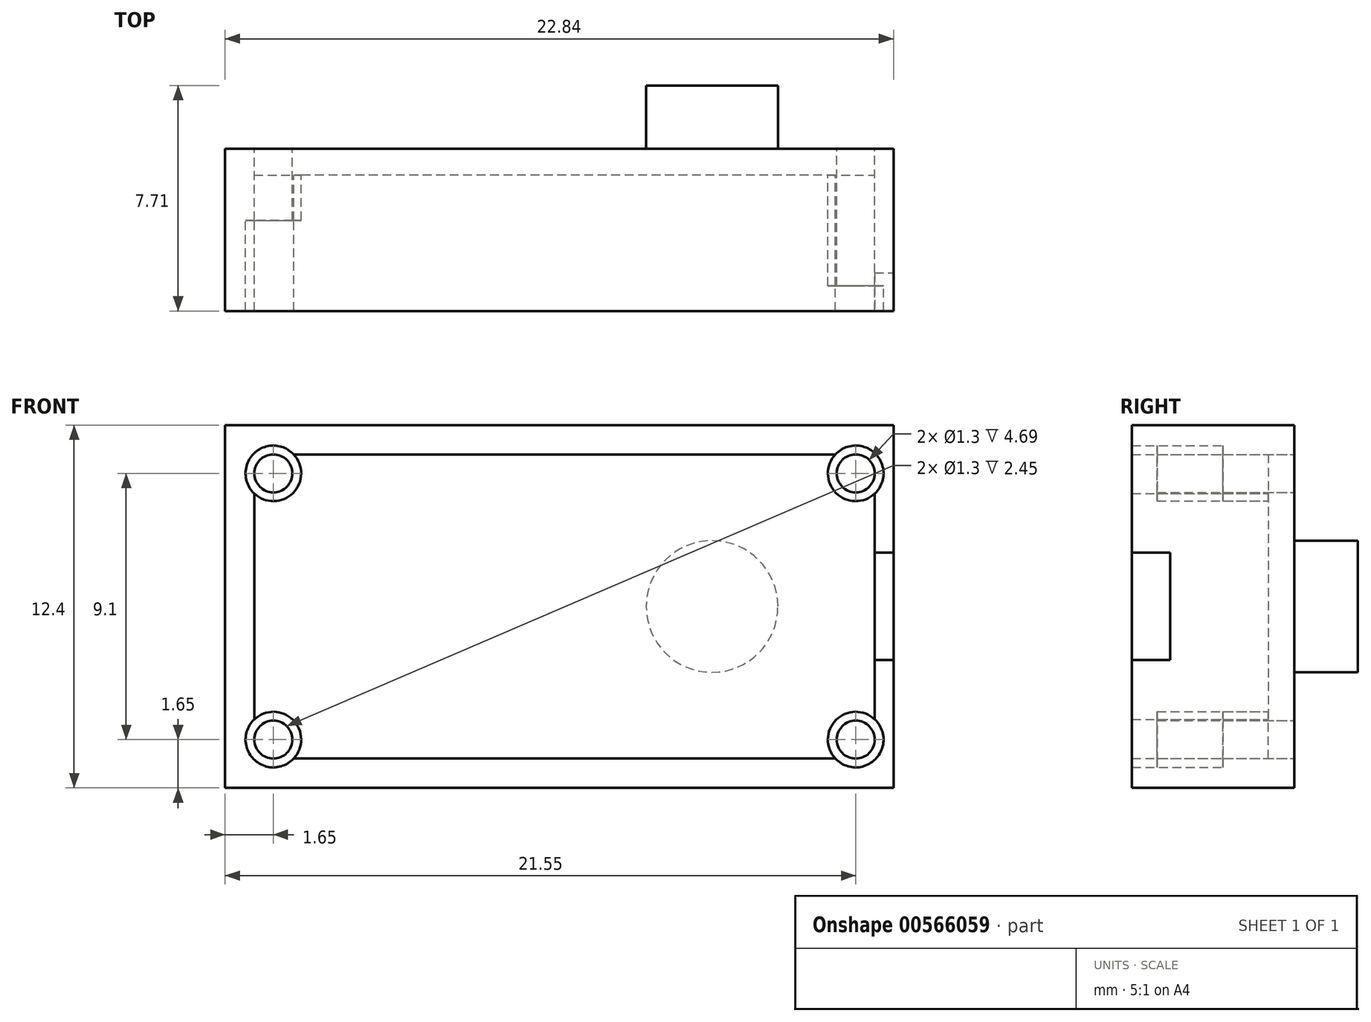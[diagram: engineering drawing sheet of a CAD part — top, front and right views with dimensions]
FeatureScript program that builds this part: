
annotation { "Feature Type Name" : "Feature", "Feature Type Description" : "" }
export const myFeature = defineFeature(function(context is Context, id is Id, definition is map)
    precondition{}
    {
        {
            var Q0;
            Q0=qCreatedBy(makeId("Front.planeOp"),FACE);
            var sketch = newSketch(context, id + "F0", { "sketchPlane" : qUnion([Q0])});
            skLineSegment(sketch, "E0.bottom", {"start": v(11.42, 6.2) * mm, "end": v(-11.42, 6.2) * mm});
            skLineSegment(sketch, "E0.top", {"start": v(11.42, -6.2) * mm, "end": v(-11.42, -6.2) * mm});
            skLineSegment(sketch, "E0.left", {"start": v(11.42, 6.2) * mm, "end": v(11.42, -6.2) * mm});
            skLineSegment(sketch, "E0.right", {"start": v(-11.42, 6.2) * mm, "end": v(-11.42, -6.2) * mm});
            skPoint(sketch, "E0.middle", {"position": v(0, 0) * mm});
            skLineSegment(sketch, "E1.0", {"start": v(10.78, 4.55) * mm, "end": v(10.78, -4.55) * mm});
            skLineSegment(sketch, "E2.0", {"start": v(10.13, -5.2) * mm, "end": v(-9.77, -5.2) * mm});
            skLineSegment(sketch, "E2.1", {"start": v(-10.42, 4.55) * mm, "end": v(-10.42, -4.55) * mm});
            skLineSegment(sketch, "E2.2", {"start": v(10.13, 5.2) * mm, "end": v(-9.77, 5.2) * mm});
            skCircle(sketch, "E3", {"center": v(10.13, 4.55) * mm, "radius": 0.95 * mm});
            skCircle(sketch, "E4", {"center": v(10.13, 4.55) * mm, "radius": 0.65 * mm});
            skLineSegment(sketch, "E5", {"start": v(24.28, 3.64) * mm, "end": v(-23.65, 3.64) * mm, "construction": true});
            skLineSegment(sketch, "E6.MirrorCS", {"start": v(24.28, -3.64) * mm, "end": v(-23.65, -3.64) * mm, "construction": true});
            skLineSegment(sketch, "E7", {"start": v(9.24, 9.62) * mm, "end": v(9.24, -10.31) * mm, "construction": true});
            skLineSegment(sketch, "E8", {"start": v(-9.1, 8.85) * mm, "end": v(-9.1, -9.67) * mm, "construction": true});
            skCircle(sketch, "E9", {"center": v(-9.77, 4.55) * mm, "radius": 0.95 * mm});
            skCircle(sketch, "E10", {"center": v(-9.77, 4.55) * mm, "radius": 0.65 * mm});
            skPoint(sketch, "E11", {"position": v(10.13, 5.2) * mm});
            skPoint(sketch, "E12", {"position": v(10.78, 4.55) * mm});
            skPoint(sketch, "E13", {"position": v(-10.42, 4.55) * mm});
            skPoint(sketch, "E14", {"position": v(-9.77, 5.2) * mm});
            skCircle(sketch, "E15.MirrorC", {"center": v(-9.77, -4.55) * mm, "radius": 0.65 * mm});
            skPoint(sketch, "E16.MirrorP", {"position": v(-9.77, -5.2) * mm});
            skCircle(sketch, "E17.MirrorC", {"center": v(-9.77, -4.55) * mm, "radius": 0.95 * mm});
            skPoint(sketch, "E18.MirrorP", {"position": v(-10.42, -4.55) * mm});
            skPoint(sketch, "E19.MirrorP", {"position": v(10.13, -5.2) * mm});
            skPoint(sketch, "E20.MirrorP", {"position": v(10.78, -4.55) * mm});
            skCircle(sketch, "E21.MirrorC", {"center": v(10.13, -4.55) * mm, "radius": 0.65 * mm});
            skCircle(sketch, "E22.MirrorC", {"center": v(10.13, -4.55) * mm, "radius": 0.95 * mm});
            skCircle(sketch, "E23", {"center": v(5.22, 0) * mm, "radius": 6.2 * mm, "construction": true});
            skPoint(sketch, "E24", {"position": v(11.42, 0) * mm});
            skCircle(sketch, "E25", {"center": v(5.22, 0) * mm, "radius": 2.25 * mm});
            skSolve(sketch);
        }
        {
            var Q0;
            Q0=makeQuery(id+"F0.imprint","IMPRINT",FACE,{"disambiguationData":[TD([[makeQuery(id+"F0.imprint","IMPRINT",EDGE,{"derivedFrom":sQuery(id+"F0.wireOp",EDGE,"E0.bottom")}),1.0]])]});
            extrude(context, id + "F1", {"entities" : qUnion([Q0]), "flatOperationType" : FlatOperationType.REMOVE, "depth" : 5.55 * mm, "offsetDistance" : 25 * mm, "domain" : OperationDomain.MODEL});
        }
        {
            var Q0;
            {var subQ0=sQuery(id+"F0.wireOp",EDGE,"E3");var subQ10=sQuery(id+"F0.wireOp",EDGE,"E1.0");var subQ15=makeQuery(id+"F0.imprint","INTERSECT",VERTEX,{"derivedFrom":[subQ10,subQ0]});Q0=makeQuery(id+"F0.imprint","IMPRINT",FACE,{"disambiguationData":[TD([[makeQuery(id+"F0.imprint","IMPRINT",EDGE,{"disambiguationData":[TD([[subQ15,-1.0]])],"derivedFrom":subQ10}),-1.0]])]});}
            extrude(context, id + "F2", {"entities" : qUnion([Q0]), "operationType" : NewBodyOperationType.ADD, "flatOperationType" : FlatOperationType.REMOVE, "depth" : 0.9 * mm, "offsetDistance" : 25 * mm, "domain" : OperationDomain.MODEL});
        }
        {
            var Q0;
            {var subQ0=sQuery(id+"F0.wireOp",EDGE,"E4");var subQ1=sQuery(id+"F0.wireOp",EDGE,"E1.0");var subQ2=makeQuery(id+"F0.imprint","INTERSECT",VERTEX,{"derivedFrom":[subQ1,subQ0]});Q0=makeQuery(id+"F0.imprint","IMPRINT",FACE,{"disambiguationData":[TD([[makeQuery(id+"F0.imprint","IMPRINT",EDGE,{"disambiguationData":[TD([[subQ2,-1.0]])],"derivedFrom":subQ1}),-1.0]])]});}
            var Q1;
            {var subQ0=sQuery(id+"F0.wireOp",EDGE,"E4");var subQ1=sQuery(id+"F0.wireOp",EDGE,"E1.0");var subQ2=makeQuery(id+"F0.imprint","INTERSECT",VERTEX,{"derivedFrom":[subQ1,subQ0]});Q1=makeQuery(id+"F0.imprint","IMPRINT",FACE,{"disambiguationData":[TD([[makeQuery(id+"F0.imprint","IMPRINT",EDGE,{"disambiguationData":[TD([[subQ2,-1.0]])],"derivedFrom":subQ1}),1.0]])]});}
            var Q2;
            {var subQ0=sQuery(id+"F0.wireOp",EDGE,"E21.MirrorC");var subQ1=sQuery(id+"F0.wireOp",EDGE,"E1.0");var subQ2=makeQuery(id+"F0.imprint","INTERSECT",VERTEX,{"derivedFrom":[subQ1,subQ0]});Q2=makeQuery(id+"F0.imprint","IMPRINT",FACE,{"disambiguationData":[TD([[makeQuery(id+"F0.imprint","IMPRINT",EDGE,{"disambiguationData":[TD([[subQ2,1.0]])],"derivedFrom":subQ1}),-1.0]])]});}
            var Q3;
            {var subQ0=sQuery(id+"F0.wireOp",EDGE,"E21.MirrorC");var subQ1=sQuery(id+"F0.wireOp",EDGE,"E1.0");var subQ2=makeQuery(id+"F0.imprint","INTERSECT",VERTEX,{"derivedFrom":[subQ1,subQ0]});Q3=makeQuery(id+"F0.imprint","IMPRINT",FACE,{"disambiguationData":[TD([[makeQuery(id+"F0.imprint","IMPRINT",EDGE,{"disambiguationData":[TD([[subQ2,1.0]])],"derivedFrom":subQ1}),1.0]])]});}
            var Q4;
            Q4 = qSketchRegion(id + "F5", true);
            extrude(context, id + "F3", {"entities" : qUnion([Q0, Q1, Q2, Q3, Q4]), "operationType" : NewBodyOperationType.ADD, "flatOperationType" : FlatOperationType.REMOVE, "depth" : 4.7 * mm, "offsetDistance" : 25 * mm, "domain" : OperationDomain.MODEL});
        }
        {
            var Q0;
            {var subQ0=sQuery(id+"F0.wireOp",EDGE,"E10");var subQ1=sQuery(id+"F0.wireOp",EDGE,"E2.1");var subQ2=makeQuery(id+"F0.imprint","INTERSECT",VERTEX,{"derivedFrom":[subQ1,subQ0]});Q0=makeQuery(id+"F0.imprint","IMPRINT",FACE,{"disambiguationData":[TD([[makeQuery(id+"F0.imprint","IMPRINT",EDGE,{"disambiguationData":[TD([[subQ2,-1.0]])],"derivedFrom":subQ1}),-1.0]])]});}
            var Q1;
            {var subQ0=sQuery(id+"F0.wireOp",EDGE,"E10");var subQ1=sQuery(id+"F0.wireOp",EDGE,"E2.1");var subQ2=makeQuery(id+"F0.imprint","INTERSECT",VERTEX,{"derivedFrom":[subQ1,subQ0]});Q1=makeQuery(id+"F0.imprint","IMPRINT",FACE,{"disambiguationData":[TD([[makeQuery(id+"F0.imprint","IMPRINT",EDGE,{"disambiguationData":[TD([[subQ2,-1.0]])],"derivedFrom":subQ1}),1.0]])]});}
            var Q2;
            {var subQ0=sQuery(id+"F0.wireOp",EDGE,"E15.MirrorC");var subQ1=sQuery(id+"F0.wireOp",EDGE,"E2.0");var subQ2=makeQuery(id+"F0.imprint","INTERSECT",VERTEX,{"derivedFrom":[subQ1,subQ0]});Q2=makeQuery(id+"F0.imprint","IMPRINT",FACE,{"disambiguationData":[TD([[makeQuery(id+"F0.imprint","IMPRINT",EDGE,{"disambiguationData":[TD([[subQ2,1.0]])],"derivedFrom":subQ1}),1.0]])]});}
            var Q3;
            {var subQ0=sQuery(id+"F0.wireOp",EDGE,"E15.MirrorC");var subQ1=sQuery(id+"F0.wireOp",EDGE,"E2.0");var subQ2=makeQuery(id+"F0.imprint","INTERSECT",VERTEX,{"derivedFrom":[subQ1,subQ0]});Q3=makeQuery(id+"F0.imprint","IMPRINT",FACE,{"disambiguationData":[TD([[makeQuery(id+"F0.imprint","IMPRINT",EDGE,{"disambiguationData":[TD([[subQ2,1.0]])],"derivedFrom":subQ1}),-1.0]])]});}
            extrude(context, id + "F4", {"entities" : qUnion([Q0, Q1, Q2, Q3]), "operationType" : NewBodyOperationType.ADD, "flatOperationType" : FlatOperationType.REMOVE, "depth" : 2.45 * mm, "offsetDistance" : 25 * mm, "domain" : OperationDomain.MODEL});
        }
        {
            var Q0;
            Q0=makeQuery(id+"F1.opExtrude","SWEPT_FACE",FACE,{"disambiguationData":[OSD([sQuery(id+"F0.wireOp",EDGE,"E0.left")])]});
            var sketch = newSketch(context, id + "F5", { "sketchPlane" : qUnion([Q0])});
            skLineSegment(sketch, "E26.bottom", {"start": v(-4.25, 1.83) * mm, "end": v(-5.55, 1.83) * mm});
            skLineSegment(sketch, "E26.top", {"start": v(-4.25, -1.83) * mm, "end": v(-5.55, -1.83) * mm});
            skLineSegment(sketch, "E26.left", {"start": v(-4.25, 1.83) * mm, "end": v(-4.25, -1.83) * mm});
            skLineSegment(sketch, "E26.right", {"start": v(-5.55, 1.83) * mm, "end": v(-5.55, -1.83) * mm});
            skPoint(sketch, "E26.middle", {"position": v(-4.9, 0) * mm});
            skSolve(sketch);
        }
        {
            var Q0;
            Q0 = qSketchRegion(id + "F5", true);
            extrude(context, id + "F6", {"entities" : qUnion([Q0]), "operationType" : NewBodyOperationType.REMOVE, "flatOperationType" : FlatOperationType.REMOVE, "depth" : -1 * mm, "offsetDistance" : 25 * mm, "domain" : OperationDomain.MODEL});
        }
        {
            var Q0;
            Q0=makeQuery(id+"F0.imprint","IMPRINT",FACE,{"disambiguationData":[TD([[makeQuery(id+"F0.imprint","IMPRINT",EDGE,{"derivedFrom":sQuery(id+"F0.wireOp",EDGE,"E25")}),1.0]])]});
            var Q1;
            Q1=sQuery(id+"F0.wireOp",EDGE,"E25");
            extrude(context, id + "F7", {"entities" : qUnion([Q0]), "flatOperationType" : FlatOperationType.REMOVE, "surfaceEntities" : qUnion([Q1]), "depth" : 0.9 * mm, "offsetDistance" : 25 * mm, "domain" : OperationDomain.MODEL});
        }
        {
            var Q0;
            Q0=makeQuery(id+"F7.opExtrude","CAP_FACE",FACE,{"disambiguationData":[OSD([sQuery(id+"F0.wireOp",EDGE,"E25")])],"isStart":false});
            extrude(context, id + "F8", {"entities" : qUnion([Q0]), "operationType" : NewBodyOperationType.ADD, "flatOperationType" : FlatOperationType.REMOVE, "oppositeDirection" : true, "depth" : 3.06 * mm, "offsetDistance" : 25 * mm, "domain" : OperationDomain.MODEL});
        }
    });
